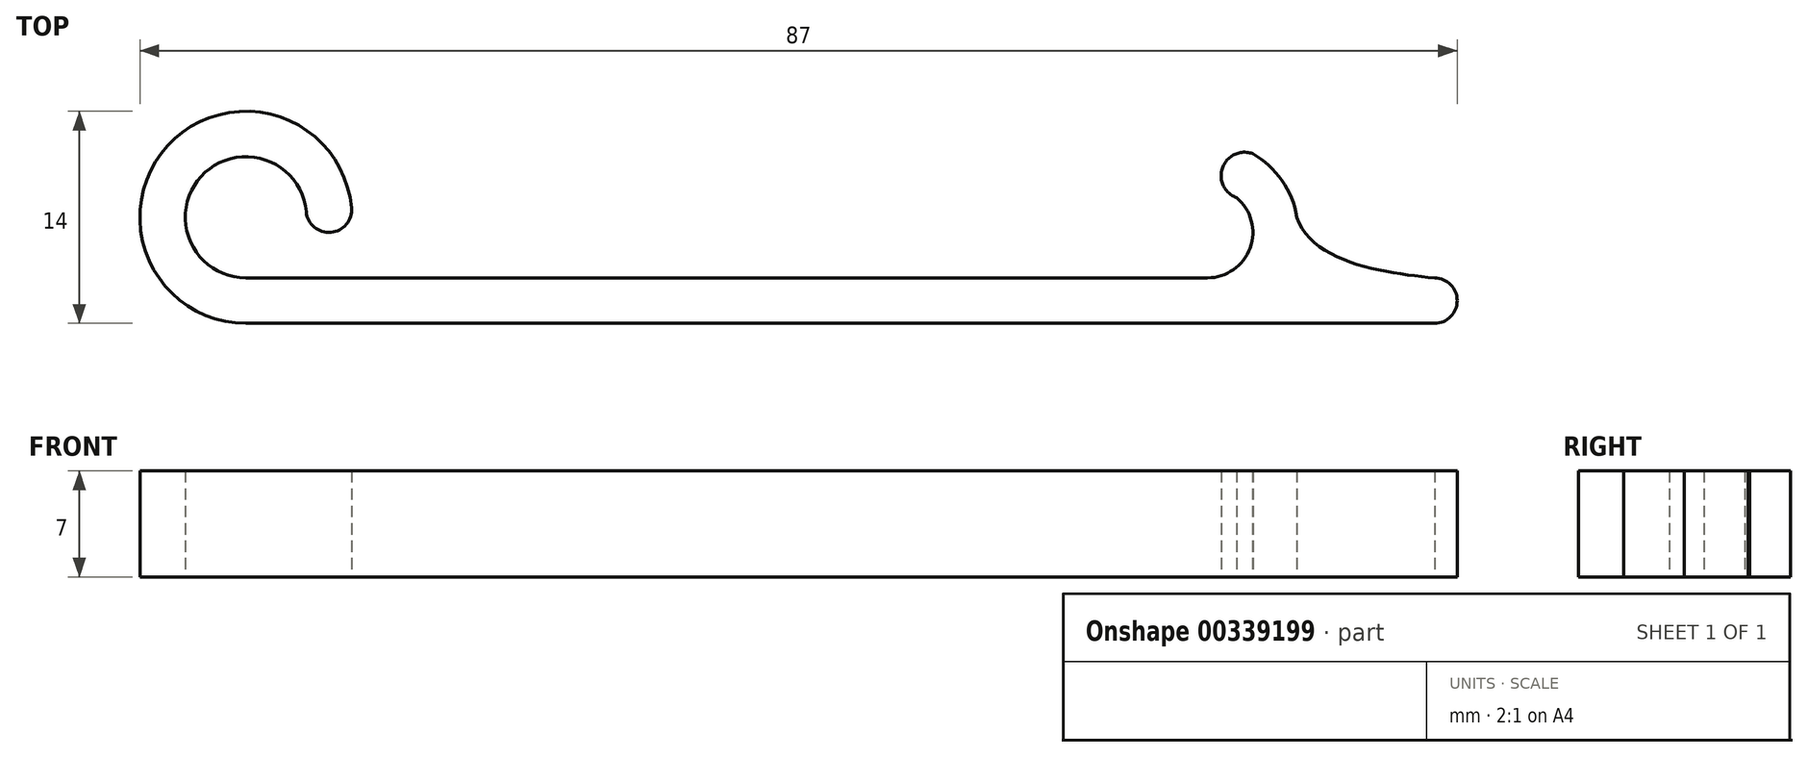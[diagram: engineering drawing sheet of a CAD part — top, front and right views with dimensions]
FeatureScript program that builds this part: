
annotation { "Feature Type Name" : "Feature", "Feature Type Description" : "" }
export const myFeature = defineFeature(function(context is Context, id is Id, definition is map)
    precondition{}
    {
        {
            var Q0;
            Q0=qCreatedBy(makeId("Top.planeOp"),FACE);
            var sketch = newSketch(context, id + "F0", { "sketchPlane" : qUnion([Q0])});
            skLineSegment(sketch, "E0", {"start": v(-31.75, 0) * mm, "end": v(31.75, 0) * mm});
            skArc(sketch, "E1", {"start": v(-31.75, 0) * mm, "mid": v(-34.7, 6.7) * mm, "end": v(-27.77, 4.36) * mm});
            skLineSegment(sketch, "E2", {"start": v(0, -19.75) * mm, "end": v(0, 14.7) * mm, "construction": true});
            skArc(sketch, "E3.MirrorCS", {"start": v(31.75, 0) * mm, "mid": v(34.57, 1.97) * mm, "end": v(33.68, 5.3) * mm});
            skArc(sketch, "E4.0", {"start": v(-31.75, -3) * mm, "mid": v(-36.92, 8.72) * mm, "end": v(-24.78, 4.64) * mm});
            skLineSegment(sketch, "E4.1", {"start": v(-31.75, -3) * mm, "end": v(31.75, -3) * mm});
            skArc(sketch, "E4.2", {"start": v(31.75, -3) * mm, "mid": v(37.55, 1.45) * mm, "end": v(34.74, 8.2) * mm});
            skLineSegment(sketch, "E5.MirrorCS", {"start": v(31.75, -3) * mm, "end": v(46.75, -3) * mm});
            skArc(sketch, "E6.MirrorCS", {"start": v(46.75, -3) * mm, "mid": v(48.25, -1.5) * mm, "end": v(46.75, 0) * mm});
            skArc(sketch, "E7.MirrorCS", {"start": v(34.74, 8.2) * mm, "mid": v(32.75, 7.28) * mm, "end": v(33.68, 5.3) * mm});
            skArc(sketch, "E8", {"start": v(-27.77, 4.36) * mm, "mid": v(-26.14, 3) * mm, "end": v(-24.78, 4.64) * mm});
            skLineSegment(sketch, "E9", {"start": v(31.75, -3) * mm, "end": v(31.75, 27.96) * mm, "construction": true});
            skLineSegment(sketch, "E10", {"start": v(-31.75, 4) * mm, "end": v(-21.72, 4.92) * mm, "construction": true});
            skFitSpline(sketch, "E11", {"points": [v(37.62, 4.17) * mm, v(46.75, 0) * mm], "startDerivative": vector(2.57, -9.57) * mm, "endDerivative": vector(9.53, -0.9) * mm});
            skLineSegment(sketch, "E12", {"start": v(31.75, 0) * mm, "end": v(38.25, 17.85) * mm, "construction": true});
            skLineSegment(sketch, "E13", {"start": v(46.75, -3) * mm, "end": v(46.75, 5.18) * mm, "construction": true});
            skSolve(sketch);
        }
        {
            var Q0;
            Q0 = qSketchRegion(id + "F0", true);
            extrude(context, id + "F1", {"entities" : qUnion([Q0]), "depth" : 7 * mm});
        }
    });
